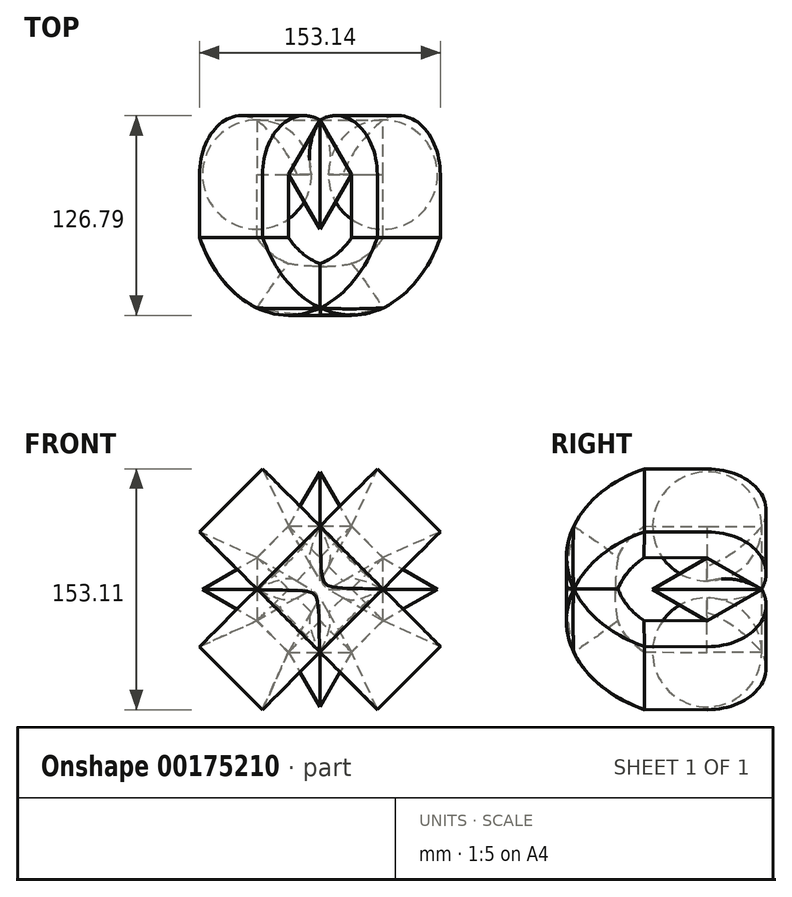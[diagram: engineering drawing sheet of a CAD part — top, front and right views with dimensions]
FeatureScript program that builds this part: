
annotation { "Feature Type Name" : "Feature", "Feature Type Description" : "" }
export const myFeature = defineFeature(function(context is Context, id is Id, definition is map)
    precondition{}
    {
        {
            var Q0;
            Q0=qCreatedBy(makeId("Front.planeOp"),FACE);
            var sketch = newSketch(context, id + "F0", { "sketchPlane" : qUnion([Q0])});
            skLineSegment(sketch, "E0.bottom", {"start": v(40, -40) * mm, "end": v(-40, -40) * mm});
            skLineSegment(sketch, "E0.top", {"start": v(40, 40) * mm, "end": v(-40, 40) * mm});
            skLineSegment(sketch, "E0.left", {"start": v(40, -40) * mm, "end": v(40, 40) * mm});
            skLineSegment(sketch, "E0.right", {"start": v(-40, -40) * mm, "end": v(-40, 40) * mm});
            skPoint(sketch, "E0.middle", {"position": v(0, 0) * mm});
            skLineSegment(sketch, "E1", {"start": v(-40, 40) * mm, "end": v(40, -40) * mm});
            skLineSegment(sketch, "E2", {"start": v(40, 40) * mm, "end": v(-40, -40) * mm});
            skSolve(sketch);
        }
        {
            var Q0;
            Q0=qCreatedBy(makeId("Right.planeOp"),FACE);
            cPlane(context, id + "F1", {"entities" : qUnion([Q0]), "cplaneType" : CPlaneType.OFFSET, "offset" : 40 * mm, "width" : 150 * mm, "height" : 150 * mm});
        }
        {
            var Q0;
            Q0=qCreatedBy(makeId("Right.planeOp"),FACE);
            cPlane(context, id + "F2", {"entities" : qUnion([Q0]), "cplaneType" : CPlaneType.OFFSET, "offset" : 40 * mm, "oppositeDirection" : true, "width" : 150 * mm, "height" : 150 * mm});
        }
        {
            var Q0;
            Q0=qCreatedBy(id+"F2.planeOp",FACE);
            var sketch = newSketch(context, id + "F3", { "sketchPlane" : qUnion([Q0])});
            skLineSegment(sketch, "E3", {"start": v(34.64, 0) * mm, "end": v(0, -20) * mm});
            skLineSegment(sketch, "E4", {"start": v(0, -20) * mm, "end": v(0, 20) * mm});
            skLineSegment(sketch, "E5", {"start": v(0, 20) * mm, "end": v(34.64, 0) * mm});
            skSolve(sketch);
        }
        {
            var Q0;
            Q0=qCreatedBy(id+"F1.planeOp",FACE);
            var sketch = newSketch(context, id + "F4", { "sketchPlane" : qUnion([Q0])});
            skLineSegment(sketch, "E6", {"start": v(34.64, 0) * mm, "end": v(0, 20) * mm});
            skLineSegment(sketch, "E7", {"start": v(0, 20) * mm, "end": v(0, -20) * mm});
            skLineSegment(sketch, "E8", {"start": v(0, -20) * mm, "end": v(34.64, 0) * mm});
            skSolve(sketch);
        }
        {
            var Q0;
            Q0=qCreatedBy(makeId("Top.planeOp"),FACE);
            cPlane(context, id + "F5", {"entities" : qUnion([Q0]), "cplaneType" : CPlaneType.OFFSET, "offset" : 40 * mm, "width" : 150 * mm, "height" : 150 * mm});
        }
        {
            var Q0;
            Q0=qCreatedBy(makeId("Top.planeOp"),FACE);
            cPlane(context, id + "F6", {"entities" : qUnion([Q0]), "cplaneType" : CPlaneType.OFFSET, "offset" : 40 * mm, "oppositeDirection" : true, "width" : 150 * mm, "height" : 150 * mm});
        }
        {
            var Q0;
            Q0=qCreatedBy(id+"F6.planeOp",FACE);
            var sketch = newSketch(context, id + "F7", { "sketchPlane" : qUnion([Q0])});
            skLineSegment(sketch, "E9", {"start": v(0, 34.64) * mm, "end": v(20, 0) * mm});
            skLineSegment(sketch, "E10", {"start": v(20, 0) * mm, "end": v(-20, 0) * mm});
            skLineSegment(sketch, "E11", {"start": v(-20, 0) * mm, "end": v(0, 34.64) * mm});
            skSolve(sketch);
        }
        {
            var Q0;
            Q0=qCreatedBy(id+"F5.planeOp",FACE);
            var sketch = newSketch(context, id + "F8", { "sketchPlane" : qUnion([Q0])});
            skLineSegment(sketch, "E12", {"start": v(0, 34.64) * mm, "end": v(-20, 0) * mm});
            skLineSegment(sketch, "E13", {"start": v(-20, 0) * mm, "end": v(20, 0) * mm});
            skLineSegment(sketch, "E14", {"start": v(20, 0) * mm, "end": v(0, 34.64) * mm});
            skSolve(sketch);
        }
        {
            var Q0;
            Q0=makeQuery(id+"F3.imprint","IMPRINT",FACE,{"disambiguationData":[TD([[makeQuery(id+"F3.imprint","IMPRINT",EDGE,{"derivedFrom":sQuery(id+"F3.wireOp",EDGE,"E3")}),-1.0]])]});
            var Q1;
            Q1=makeQuery(id+"F8.imprint","IMPRINT",FACE,{"disambiguationData":[TD([[makeQuery(id+"F8.imprint","IMPRINT",EDGE,{"derivedFrom":sQuery(id+"F8.wireOp",EDGE,"E12")}),1.0]])]});
            loft(context, id + "F9", {"sheetProfilesArray" : [{ "sheetProfileEntities" : qUnion([Q0]) }, { "sheetProfileEntities" : qUnion([Q1]) }]});
        }
        {
            var Q0;
            Q0=makeQuery(id+"F4.imprint","IMPRINT",FACE,{"disambiguationData":[TD([[makeQuery(id+"F4.imprint","IMPRINT",EDGE,{"derivedFrom":sQuery(id+"F4.wireOp",EDGE,"E6")}),1.0]])]});
            var Q1;
            Q1=makeQuery(id+"F7.imprint","IMPRINT",FACE,{"disambiguationData":[TD([[makeQuery(id+"F7.imprint","IMPRINT",EDGE,{"derivedFrom":sQuery(id+"F7.wireOp",EDGE,"E9")}),-1.0]])]});
            loft(context, id + "F10", {"sheetProfilesArray" : [{ "sheetProfileEntities" : qUnion([Q0]) }, { "sheetProfileEntities" : qUnion([Q1]) }]});
        }
        {
            var Q0;
            Q0=makeQuery(id+"F7.imprint","IMPRINT",FACE,{"disambiguationData":[TD([[makeQuery(id+"F7.imprint","IMPRINT",EDGE,{"derivedFrom":sQuery(id+"F7.wireOp",EDGE,"E9")}),-1.0]])]});
            var Q1;
            Q1=makeQuery(id+"F3.imprint","IMPRINT",FACE,{"disambiguationData":[TD([[makeQuery(id+"F3.imprint","IMPRINT",EDGE,{"derivedFrom":sQuery(id+"F3.wireOp",EDGE,"E3")}),-1.0]])]});
            loft(context, id + "F11", {"sheetProfilesArray" : [{ "sheetProfileEntities" : qUnion([Q0]) }, { "sheetProfileEntities" : qUnion([Q1]) }]});
        }
        {
            var Q0;
            Q0=makeQuery(id+"F8.imprint","IMPRINT",FACE,{"disambiguationData":[TD([[makeQuery(id+"F8.imprint","IMPRINT",EDGE,{"derivedFrom":sQuery(id+"F8.wireOp",EDGE,"E12")}),1.0]])]});
            var Q1;
            Q1=makeQuery(id+"F10.opLoft","CAP_FACE",FACE,{"disambiguationData":[OSD([makeQuery(id+"F4.imprint","IMPRINT",FACE,{"disambiguationData":[TD([[makeQuery(id+"F4.imprint","IMPRINT",EDGE,{"derivedFrom":sQuery(id+"F4.wireOp",EDGE,"E6")}),1.0]])]})])],"isStart":true});
            loft(context, id + "F12", {"sheetProfilesArray" : [{ "sheetProfileEntities" : qUnion([Q0]) }, { "sheetProfileEntities" : qUnion([Q1]) }]});
        }
        {
            var Q0;
            Q0=makeQuery(id+"F7.imprint","IMPRINT",FACE,{"disambiguationData":[TD([[makeQuery(id+"F7.imprint","IMPRINT",EDGE,{"derivedFrom":sQuery(id+"F7.wireOp",EDGE,"E9")}),-1.0]])]});
            var Q1;
            Q1=sQuery(id+"F7.wireOp",EDGE,"E10");
            revolve(context, id + "F13", {"operationType" : NewBodyOperationType.ADD, "entities" : qUnion([Q0]), "axis" : qUnion([Q1]), "revolveType" : RevolveType.FULL});
        }
        {
            var Q0;
            Q0=makeQuery(id+"F10.opLoft","CAP_FACE",FACE,{"disambiguationData":[OSD([makeQuery(id+"F4.imprint","IMPRINT",FACE,{"disambiguationData":[TD([[makeQuery(id+"F4.imprint","IMPRINT",EDGE,{"derivedFrom":sQuery(id+"F4.wireOp",EDGE,"E6")}),1.0]])]})])],"isStart":true});
            var Q1;
            Q1=sQuery(id+"F0.wireOp",EDGE,"E0.left");
            revolve(context, id + "F14", {"operationType" : NewBodyOperationType.ADD, "entities" : qUnion([Q0]), "axis" : qUnion([Q1]), "revolveType" : RevolveType.FULL});
        }
        {
            var Q0;
            Q0=makeQuery(id+"F3.imprint","IMPRINT",FACE,{"disambiguationData":[TD([[makeQuery(id+"F3.imprint","IMPRINT",EDGE,{"derivedFrom":sQuery(id+"F3.wireOp",EDGE,"E3")}),-1.0]])]});
            var Q1;
            Q1=sQuery(id+"F3.wireOp",EDGE,"E4");
            revolve(context, id + "F15", {"operationType" : NewBodyOperationType.ADD, "entities" : qUnion([Q0]), "axis" : qUnion([Q1]), "revolveType" : RevolveType.FULL});
        }
        {
            var Q0;
            Q0=makeQuery(id+"F8.imprint","IMPRINT",FACE,{"disambiguationData":[TD([[makeQuery(id+"F8.imprint","IMPRINT",EDGE,{"derivedFrom":sQuery(id+"F8.wireOp",EDGE,"E12")}),1.0]])]});
            var Q1;
            Q1=sQuery(id+"F8.wireOp",EDGE,"E13");
            revolve(context, id + "F16", {"operationType" : NewBodyOperationType.ADD, "entities" : qUnion([Q0]), "axis" : qUnion([Q1]), "revolveType" : RevolveType.FULL});
        }
        {
            var Q0;
            {var subQ0=sQuery(id+"F7.wireOp",EDGE,"E9");var subQ1=sQuery(id+"F7.wireOp",EDGE,"E10");var subQ2=sQuery(id+"F7.wireOp",EDGE,"E11");var subQ3=sQuery(id+"F4.wireOp",EDGE,"E8");var subQ4=sQuery(id+"F4.wireOp",EDGE,"E7");var subQ5=sQuery(id+"F4.wireOp",EDGE,"E6");Q0=makeQuery(id+"F10.opLoft","SWEPT_FACE",FACE,{"disambiguationData":[OSD([subQ5,subQ4,subQ3,subQ0,subQ1,subQ2]),TDD([makeQuery(id+"F4.imprint","INTERSECT",VERTEX,{"derivedFrom":[subQ5,subQ3]}),makeQuery(id+"F4.imprint","INTERSECT",VERTEX,{"derivedFrom":[subQ4,subQ3]}),makeQuery(id+"F4.imprint","IMPRINT",EDGE,{"derivedFrom":subQ3}),makeQuery(id+"F7.imprint","INTERSECT",VERTEX,{"derivedFrom":[subQ0,subQ2]}),makeQuery(id+"F7.imprint","INTERSECT",VERTEX,{"derivedFrom":[subQ0,subQ1]}),makeQuery(id+"F7.imprint","IMPRINT",EDGE,{"derivedFrom":subQ0})])]});}
            var Q1;
            Q1=makeQuery(id+"F10.opLoft","SWEPT_EDGE",EDGE,{"disambiguationData":[OSD([sQuery(id+"F4.wireOp",EDGE,"E7"),sQuery(id+"F4.wireOp",EDGE,"E8"),sQuery(id+"F7.wireOp",EDGE,"E9"),sQuery(id+"F7.wireOp",EDGE,"E10")])]});
            revolve(context, id + "F17", {"operationType" : NewBodyOperationType.ADD, "entities" : qUnion([Q0]), "axis" : qUnion([Q1]), "revolveType" : RevolveType.ONE_DIRECTION, "angle" : 112 * degree});
        }
        {
            var Q0;
            {var subQ0=sQuery(id+"F7.wireOp",EDGE,"E11");var subQ1=sQuery(id+"F7.wireOp",EDGE,"E10");var subQ2=sQuery(id+"F7.wireOp",EDGE,"E9");var subQ3=sQuery(id+"F3.wireOp",EDGE,"E3");var subQ4=sQuery(id+"F3.wireOp",EDGE,"E4");var subQ5=sQuery(id+"F3.wireOp",EDGE,"E5");Q0=makeQuery(id+"F11.opLoft","SWEPT_FACE",FACE,{"disambiguationData":[OSD([subQ3,subQ4,subQ5,subQ2,subQ1,subQ0]),TDD([makeQuery(id+"F3.imprint","INTERSECT",VERTEX,{"derivedFrom":[subQ3,subQ5]}),makeQuery(id+"F3.imprint","INTERSECT",VERTEX,{"derivedFrom":[subQ3,subQ4]}),makeQuery(id+"F3.imprint","IMPRINT",EDGE,{"derivedFrom":subQ3}),makeQuery(id+"F7.imprint","INTERSECT",VERTEX,{"derivedFrom":[subQ2,subQ0]}),makeQuery(id+"F7.imprint","INTERSECT",VERTEX,{"derivedFrom":[subQ1,subQ0]}),makeQuery(id+"F7.imprint","IMPRINT",EDGE,{"derivedFrom":subQ0})])]});}
            var Q1;
            Q1=makeQuery(id+"F11.opLoft","SWEPT_EDGE",EDGE,{"disambiguationData":[OSD([sQuery(id+"F3.wireOp",EDGE,"E3"),sQuery(id+"F3.wireOp",EDGE,"E4"),sQuery(id+"F7.wireOp",EDGE,"E10"),sQuery(id+"F7.wireOp",EDGE,"E11")])]});
            revolve(context, id + "F18", {"operationType" : NewBodyOperationType.ADD, "entities" : qUnion([Q0]), "axis" : qUnion([Q1]), "revolveType" : RevolveType.ONE_DIRECTION, "angle" : 112 * degree});
        }
        {
            var Q0;
            {var subQ0=sQuery(id+"F8.wireOp",EDGE,"E12");var subQ1=sQuery(id+"F8.wireOp",EDGE,"E13");var subQ2=sQuery(id+"F8.wireOp",EDGE,"E14");var subQ3=sQuery(id+"F3.wireOp",EDGE,"E5");var subQ4=sQuery(id+"F3.wireOp",EDGE,"E4");var subQ5=sQuery(id+"F3.wireOp",EDGE,"E3");Q0=makeQuery(id+"F9.opLoft","SWEPT_FACE",FACE,{"disambiguationData":[OSD([subQ5,subQ4,subQ3,subQ0,subQ1,subQ2]),TDD([makeQuery(id+"F3.imprint","INTERSECT",VERTEX,{"derivedFrom":[subQ5,subQ3]}),makeQuery(id+"F3.imprint","INTERSECT",VERTEX,{"derivedFrom":[subQ4,subQ3]}),makeQuery(id+"F3.imprint","IMPRINT",EDGE,{"derivedFrom":subQ3}),makeQuery(id+"F8.imprint","INTERSECT",VERTEX,{"derivedFrom":[subQ0,subQ2]}),makeQuery(id+"F8.imprint","INTERSECT",VERTEX,{"derivedFrom":[subQ0,subQ1]}),makeQuery(id+"F8.imprint","IMPRINT",EDGE,{"derivedFrom":subQ0})])]});}
            var Q1;
            Q1=makeQuery(id+"F9.opLoft","SWEPT_EDGE",EDGE,{"disambiguationData":[OSD([sQuery(id+"F3.wireOp",EDGE,"E4"),sQuery(id+"F3.wireOp",EDGE,"E5"),sQuery(id+"F8.wireOp",EDGE,"E12"),sQuery(id+"F8.wireOp",EDGE,"E13")])]});
            revolve(context, id + "F19", {"operationType" : NewBodyOperationType.ADD, "entities" : qUnion([Q0]), "axis" : qUnion([Q1]), "revolveType" : RevolveType.ONE_DIRECTION, "angle" : 112 * degree});
        }
        {
            var Q0;
            {var subQ0=sQuery(id+"F4.wireOp",EDGE,"E6");var subQ1=sQuery(id+"F4.wireOp",EDGE,"E7");var subQ2=sQuery(id+"F4.wireOp",EDGE,"E8");var subQ3=sQuery(id+"F8.wireOp",EDGE,"E14");var subQ4=sQuery(id+"F8.wireOp",EDGE,"E13");var subQ5=sQuery(id+"F8.wireOp",EDGE,"E12");Q0=makeQuery(id+"F12.opLoft","SWEPT_FACE",FACE,{"disambiguationData":[OSD([subQ0,subQ1,subQ2,subQ5,subQ4,subQ3]),TDD([makeQuery(id+"F8.imprint","INTERSECT",VERTEX,{"derivedFrom":[subQ5,subQ3]}),makeQuery(id+"F8.imprint","INTERSECT",VERTEX,{"derivedFrom":[subQ4,subQ3]}),makeQuery(id+"F8.imprint","IMPRINT",EDGE,{"derivedFrom":subQ3}),makeQuery(id+"F10.opLoft","MID_CAP_VERTEX",VERTEX,{"disambiguationData":[OSD([subQ0,subQ2])],"capPos":0.0}),makeQuery(id+"F10.opLoft","MID_CAP_VERTEX",VERTEX,{"disambiguationData":[OSD([subQ0,subQ1])],"capPos":0.0}),makeQuery(id+"F10.opLoft","MID_CAP_EDGE",EDGE,{"disambiguationData":[OSD([subQ0,subQ1,subQ2]),TDD([makeQuery(id+"F4.imprint","INTERSECT",VERTEX,{"derivedFrom":[subQ0,subQ2]}),makeQuery(id+"F4.imprint","INTERSECT",VERTEX,{"derivedFrom":[subQ0,subQ1]}),makeQuery(id+"F4.imprint","IMPRINT",EDGE,{"derivedFrom":subQ0})])],"capPos":0.0})])]});}
            var Q1;
            Q1=makeQuery(id+"F12.opLoft","SWEPT_EDGE",EDGE,{"disambiguationData":[OSD([sQuery(id+"F4.wireOp",EDGE,"E6"),sQuery(id+"F4.wireOp",EDGE,"E7"),sQuery(id+"F8.wireOp",EDGE,"E13"),sQuery(id+"F8.wireOp",EDGE,"E14")])]});
            revolve(context, id + "F20", {"operationType" : NewBodyOperationType.ADD, "entities" : qUnion([Q0]), "axis" : qUnion([Q1]), "revolveType" : RevolveType.ONE_DIRECTION, "angle" : 112 * degree});
        }
        {
            var Q0;
            Q0=makeQuery(id+"F20.opRevolve","CAP_FACE",FACE,{"disambiguationData":[OSD([sQuery(id+"F4.wireOp",EDGE,"E6"),sQuery(id+"F4.wireOp",EDGE,"E7"),sQuery(id+"F4.wireOp",EDGE,"E8"),sQuery(id+"F8.wireOp",EDGE,"E12"),sQuery(id+"F8.wireOp",EDGE,"E13"),sQuery(id+"F8.wireOp",EDGE,"E14")])],"isStart":false});
            var Q1;
            Q1=makeQuery(id+"F19.opRevolve","CAP_FACE",FACE,{"disambiguationData":[OSD([sQuery(id+"F3.wireOp",EDGE,"E3"),sQuery(id+"F3.wireOp",EDGE,"E4"),sQuery(id+"F3.wireOp",EDGE,"E5"),sQuery(id+"F8.wireOp",EDGE,"E12"),sQuery(id+"F8.wireOp",EDGE,"E13"),sQuery(id+"F8.wireOp",EDGE,"E14")])],"isStart":false});
            var Q2;
            Q2=makeQuery(id+"F18.opRevolve","CAP_FACE",FACE,{"disambiguationData":[OSD([sQuery(id+"F3.wireOp",EDGE,"E3"),sQuery(id+"F3.wireOp",EDGE,"E4"),sQuery(id+"F3.wireOp",EDGE,"E5"),sQuery(id+"F7.wireOp",EDGE,"E9"),sQuery(id+"F7.wireOp",EDGE,"E10"),sQuery(id+"F7.wireOp",EDGE,"E11")])],"isStart":false});
            var Q3;
            Q3=makeQuery(id+"F17.opRevolve","CAP_FACE",FACE,{"disambiguationData":[OSD([sQuery(id+"F4.wireOp",EDGE,"E6"),sQuery(id+"F4.wireOp",EDGE,"E7"),sQuery(id+"F4.wireOp",EDGE,"E8"),sQuery(id+"F7.wireOp",EDGE,"E9"),sQuery(id+"F7.wireOp",EDGE,"E10"),sQuery(id+"F7.wireOp",EDGE,"E11")])],"isStart":false});
            extrude(context, id + "F21", {"entities" : qUnion([Q0, Q1, Q2, Q3]), "operationType" : NewBodyOperationType.ADD, "depth" : 40 * mm});
        }
        {
            var Q0;
            Q0=makeQuery(id+"F21.opExtrude","CAP_FACE",FACE,{"disambiguationData":[OSD([sQuery(id+"F4.wireOp",EDGE,"E6"),sQuery(id+"F4.wireOp",EDGE,"E7"),sQuery(id+"F4.wireOp",EDGE,"E8"),sQuery(id+"F8.wireOp",EDGE,"E12"),sQuery(id+"F8.wireOp",EDGE,"E13"),sQuery(id+"F8.wireOp",EDGE,"E14")])],"isStart":false});
            var Q1;
            Q1=sQuery(id+"F0.wireOp",EDGE,"E1");
            revolve(context, id + "F22", {"operationType" : NewBodyOperationType.ADD, "entities" : qUnion([Q0]), "axis" : qUnion([Q1]), "revolveType" : RevolveType.ONE_DIRECTION, "angle" : 127 * degree});
        }
        {
            var Q0;
            Q0=makeQuery(id+"F21.opExtrude","CAP_FACE",FACE,{"disambiguationData":[OSD([sQuery(id+"F3.wireOp",EDGE,"E3"),sQuery(id+"F3.wireOp",EDGE,"E4"),sQuery(id+"F3.wireOp",EDGE,"E5"),sQuery(id+"F8.wireOp",EDGE,"E12"),sQuery(id+"F8.wireOp",EDGE,"E13"),sQuery(id+"F8.wireOp",EDGE,"E14")]),OD(0.0)],"isStart":false});
            var Q1;
            Q1=sQuery(id+"F0.wireOp",EDGE,"E2");
            revolve(context, id + "F23", {"operationType" : NewBodyOperationType.ADD, "entities" : qUnion([Q0]), "axis" : qUnion([Q1]), "revolveType" : RevolveType.ONE_DIRECTION, "oppositeDirection" : true, "angle" : 127 * degree});
        }
    });
